# Revit family: Washfountain_Lavatory-Bradley_Corp-SN2004-Type_B_Drain
name_source: partatom
category: Plumbing Fixtures
revit_build: Autodesk Revit MEP 2012 (Build: 20110309_2315(x64)
units: mm (PartAtom-declared; Revit-internal decimal feet)

## types (3) — shared parameters
ADA Compliant = Yes
Assembly Code = D2010300
Bowl Material = Metal - Bradley Corp - Stainless Steel - Polished
Buy American Act = No
Cold Lavatory Inlet = 1/2"
Cold Lavatory Inlet Radius = 1/4"
Description = Washfountain, 54" Semi Circular
Drain Primary = 1 1/2"
Drain Primary Radius = 3/4"
Drain Secondary = 1 1/2"
Drain Secondary Radius = 3/4"
Flow Rate = 0.5 gal/min
Frequency = 50 Hz
Hot Lavatory Inlet = 1/2"
Hot Lavatory Inlet Radius = 1/4"
Industry Standards = cUPC Certified
Manufacturer = Bradley Corp
MasterFormat Number = 22 42 16
MasterFormat Title = Commercial Lavatories and Sinks
Model = SN2004
OmniClass Table 21 Number = 21-04 20 10 60
OmniClass Table 21 Title = Plumbing Fixtures
OmniClass Table 23 Number = 23-31 13 00
OmniClass Table 23 Title = Sinks/Lavatories
Operating Water Pressure Range = 20 - 80 PSI
Pedestal Material = Metal - Bradley Corp - Stainless Steel - Polished
Product Tech Data URL - English = http://bradleycorp.com
Sensor Module Holder = 7.65 "
Specifications URL = http://www.bradleycorp.com
Towel Dispenser Holder = 4.25 "
URL = http://www.bradleycorp.com
Vent = 1 1/2"
Vent Radius = 3/4"
Version = 2.0
Voltage = 110 V
Width = 54 "
zero-valued in all types: CWFU, HWFU, WFU

## per-type parameters (varying)
| type | Pedestal Height | Rim Height | Sensor Module Height | Towel Dispenser Height |
| Standard | 29 " | 33.25 " | 42.75 " | 47 " |
| TAS | 27 " | 31.25 " | 40.75 " | 45 " |
| Juvenile | 25 " | 29.25 " | 38.75 " | 43 " |

## geometry (parser evidence)
native form markers: Blend x10, Sweep x8
no freeform markers — native parametric forms only
